# Revit family: SANINDUSA_109209004_Unu_UnuPedestalWithoutHole40_V0
name_source: partatom
category: Plumbing Fixtures
units: mm (PartAtom-declared; Revit-internal decimal feet)

## family parameters
Cut with Voids When Loaded = No
Host = Face
Part Type = Normal
Room Calculation Point = No
Round Connector Dimension = Use Diameter
Shared = No

## types (1)
- SANINDUSA_109209004_Unu_UnuPedestalWithoutHole40_V0
    AssetType = Fixed
    Color = white
    Default Elevation = 1219 mm
    Description = washbasin support appliance
    DrainSize = 0 mm  [stored 0 ft]
    Element Type = PEDESTAL: washbasin support appliance
    Finish = gloss
    Installation Instructions = https://www.tec.sanindusa.pt
    Manufacturer = Sanindusa
    ManufacturerName = Sanindusa
    ManufacturerURL = www.tec.sanindusa.pt
    Material = fine fireclay
    Model = 109209004
    ModelNumber = 109209004
    ModelReference = Unu
    Name = Unu pedestal
    NominalDepth = 0 mm  [stored 0 ft]
    NominalHeight = 630 mm  [stored 2.06693 ft]
    NominalLength = 400 mm  [stored 1.31234 ft]
    NominalWidth = 400 mm  [stored 1.31234 ft]
    ProductInformation = https://www.tec.sanindusa.pt
    ProductionYear = 2010
    Shape = round
    Size = 40
    URL = www.tec.sanindusa.pt
    Version = 1
    WarrantyDescription = https://www.tec.sanindusa.pt
    WarrantyDurationParts = 5
    WarrantyDurationUnit = year
    WashHandBasinMounting = pedestal
    Waste Connection = Yes
    Weight = 26.40 kg

note: [stored X ft] marks values corroborated as IEEE doubles in the binary element streams (Revit-internal decimal feet)

## geometry (parser evidence)
native form markers: Sweep x8
no freeform markers — native parametric forms only
